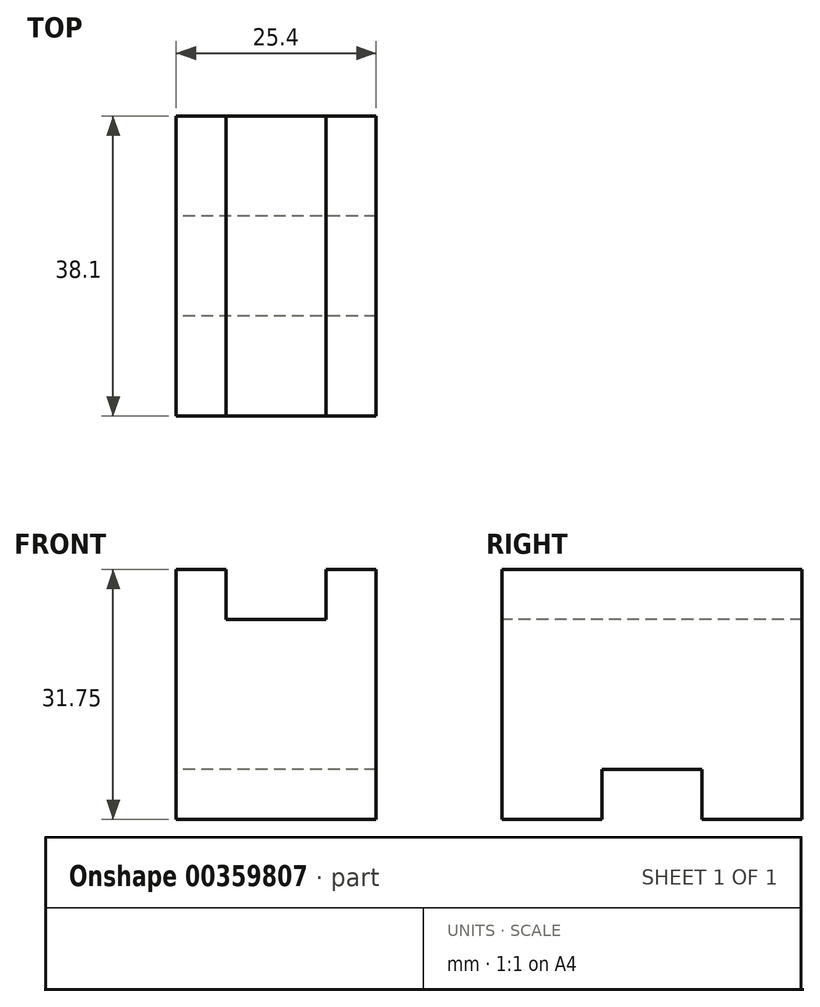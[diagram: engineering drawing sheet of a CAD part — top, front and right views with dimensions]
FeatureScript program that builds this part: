
annotation { "Feature Type Name" : "Feature", "Feature Type Description" : "" }
export const myFeature = defineFeature(function(context is Context, id is Id, definition is map)
    precondition{}
    {
        {
            var Q0;
            Q0=qCreatedBy(makeId("Right.planeOp"),FACE);
            var sketch = newSketch(context, id + "F0", { "sketchPlane" : qUnion([Q0])});
            skLineSegment(sketch, "E0", {"start": v(-16.9, 0) * mm, "end": v(-16.9, 31.75) * mm});
            skLineSegment(sketch, "E1", {"start": v(-16.9, 31.75) * mm, "end": v(21.2, 31.75) * mm});
            skLineSegment(sketch, "E2", {"start": v(21.2, 31.75) * mm, "end": v(21.2, 0) * mm});
            skLineSegment(sketch, "E3", {"start": v(21.2, 0) * mm, "end": v(-16.9, 0) * mm});
            skSolve(sketch);
        }
        {
            var Q0;
            Q0 = qSketchRegion(id + "F0", true);
            extrude(context, id + "F1", {"entities" : qUnion([Q0]), "depth" : 25.4 * mm});
        }
        {
            var Q0;
            Q0=qCreatedBy(makeId("Right.planeOp"),FACE);
            var sketch = newSketch(context, id + "F2", { "sketchPlane" : qUnion([Q0])});
            skLineSegment(sketch, "E4", {"start": v(8.5, 6.35) * mm, "end": v(-4.2, 6.35) * mm});
            skLineSegment(sketch, "E5", {"start": v(-4.2, 6.35) * mm, "end": v(-4.2, 0) * mm});
            skLineSegment(sketch, "E6", {"start": v(8.5, 6.35) * mm, "end": v(8.5, 0) * mm});
            skLineSegment(sketch, "E7", {"start": v(8.5, 0) * mm, "end": v(-4.2, 0) * mm});
            skSolve(sketch);
        }
        {
            var Q0;
            Q0=makeQuery(id+"F2.imprint","IMPRINT",FACE,{"disambiguationData":[TD([[makeQuery(id+"F2.imprint","IMPRINT",EDGE,{"derivedFrom":sQuery(id+"F2.wireOp",EDGE,"E4")}),1.0]])]});
            extrude(context, id + "F3", {"entities" : qUnion([Q0]), "operationType" : NewBodyOperationType.REMOVE, "depth" : 25.4 * mm});
        }
        {
            var Q0;
            Q0=qCreatedBy(makeId("Front.planeOp"),FACE);
            var sketch = newSketch(context, id + "F4", { "sketchPlane" : qUnion([Q0])});
            skLineSegment(sketch, "E8", {"start": v(19.05, 25.4) * mm, "end": v(6.35, 25.4) * mm});
            skLineSegment(sketch, "E9", {"start": v(6.35, 25.4) * mm, "end": v(6.35, 31.75) * mm});
            skLineSegment(sketch, "E10", {"start": v(19.05, 25.4) * mm, "end": v(19.05, 31.75) * mm});
            skLineSegment(sketch, "E11", {"start": v(6.35, 31.75) * mm, "end": v(19.05, 31.75) * mm});
            skSolve(sketch);
        }
        {
            var Q0;
            Q0 = qSketchRegion(id + "F4", true);
            extrude(context, id + "F5", {"entities" : qUnion([Q0]), "operationType" : NewBodyOperationType.REMOVE, "oppositeDirection" : true, "depth" : 25.4 * mm});
        }
        {
            var Q0;
            Q0 = qSketchRegion(id + "F4", true);
            extrude(context, id + "F6", {"entities" : qUnion([Q0]), "operationType" : NewBodyOperationType.REMOVE, "depth" : 25.4 * mm});
        }
    });
